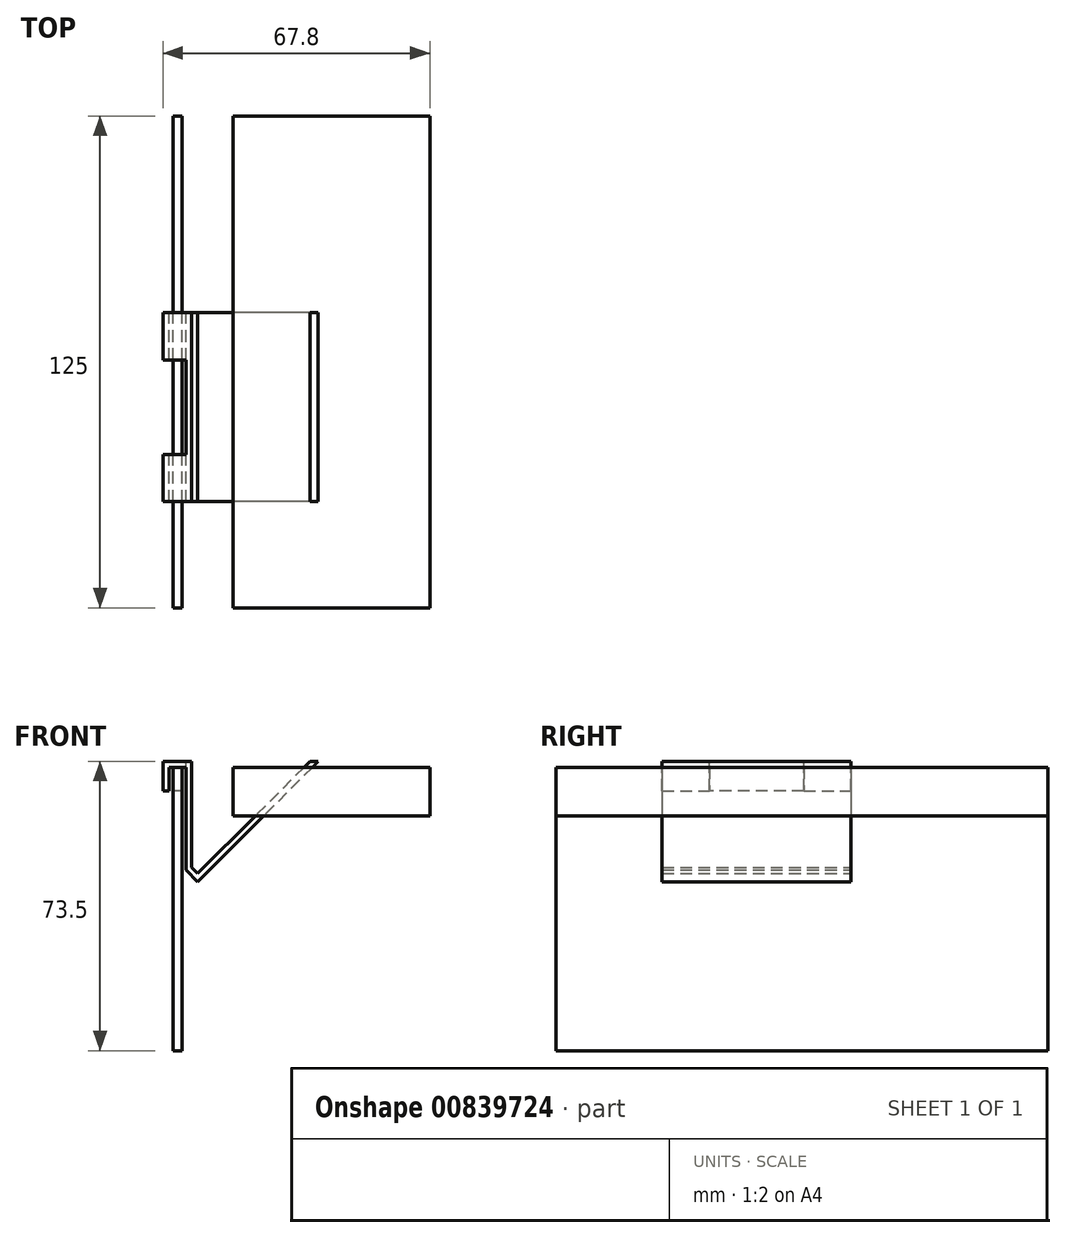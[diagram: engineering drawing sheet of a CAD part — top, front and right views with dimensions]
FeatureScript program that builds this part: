
annotation { "Feature Type Name" : "Feature", "Feature Type Description" : "" }
export const myFeature = defineFeature(function(context is Context, id is Id, definition is map)
    precondition{}
    {
        {
            var Q0;
            Q0=qCreatedBy(makeId("Front.planeOp"),FACE);
            var sketch = newSketch(context, id + "F0", { "sketchPlane" : qUnion([Q0])});
            skLineSegment(sketch, "E0", {"start": v(0, 96.34) * mm, "end": v(0, -110.81) * mm, "construction": true});
            skLineSegment(sketch, "E1", {"start": v(82.17, 0) * mm, "end": v(-88.3, 0) * mm, "construction": true});
            skSolve(sketch);
        }
        {
            var Q0;
            Q0=qCreatedBy(makeId("Front.planeOp"),FACE);
            var sketch = newSketch(context, id + "F1", { "sketchPlane" : qUnion([Q0])});
            skLineSegment(sketch, "E2.top", {"start": v(0, -72) * mm, "end": v(-2.3, -72) * mm});
            skLineSegment(sketch, "E2.left", {"start": v(0, 0) * mm, "end": v(0, -72) * mm});
            skLineSegment(sketch, "E2.right", {"start": v(-2.3, 0) * mm, "end": v(-2.3, -72) * mm});
            skLineSegment(sketch, "E3", {"start": v(-2.3, 0) * mm, "end": v(0, 0) * mm});
            skSolve(sketch);
        }
        {
            var Q0;
            Q0 = qSketchRegion(id + "F1", true);
            extrude(context, id + "F2", {"entities" : qUnion([Q0]), "depth" : 75 * mm, "offsetDistance" : 25 * mm, "hasSecondDirection" : true, "secondDirectionOppositeDirection" : true, "secondDirectionDepth" : 50 * mm});
        }
        {
            var Q0;
            Q0=qCreatedBy(makeId("Front.planeOp"),FACE);
            var sketch = newSketch(context, id + "F3", { "sketchPlane" : qUnion([Q0])});
            skLineSegment(sketch, "E4.bottom", {"start": v(13, 0) * mm, "end": v(63, 0) * mm});
            skLineSegment(sketch, "E4.top", {"start": v(13, -12.35) * mm, "end": v(63, -12.35) * mm});
            skLineSegment(sketch, "E4.left", {"start": v(13, 0) * mm, "end": v(13, -12.35) * mm});
            skLineSegment(sketch, "E4.right", {"start": v(63, 0) * mm, "end": v(63, -12.35) * mm});
            skSolve(sketch);
        }
        {
            var Q0;
            Q0 = qSketchRegion(id + "F3", true);
            extrude(context, id + "F4", {"entities" : qUnion([Q0]), "depth" : 75 * mm, "offsetDistance" : 25 * mm, "hasSecondDirection" : true, "secondDirectionOppositeDirection" : true, "secondDirectionDepth" : 50 * mm});
        }
        {
            var Q0;
            Q0=qCreatedBy(makeId("Front.planeOp"),FACE);
            var sketch = newSketch(context, id + "F5", { "sketchPlane" : qUnion([Q0])});
            skLineSegment(sketch, "E5.top", {"start": v(-4.8, -6) * mm, "end": v(-3.3, -6) * mm});
            skLineSegment(sketch, "E5.right", {"start": v(-3.3, 0) * mm, "end": v(-3.3, -6) * mm});
            skLineSegment(sketch, "E6.left", {"start": v(2.5, 1.5) * mm, "end": v(2.5, -25.5) * mm});
            skLineSegment(sketch, "E6.right", {"start": v(1, 0) * mm, "end": v(1, -26.12) * mm});
            skLineSegment(sketch, "E7", {"start": v(-4.8, 1.5) * mm, "end": v(2.5, 1.5) * mm});
            skLineSegment(sketch, "E8", {"start": v(-4.8, -6) * mm, "end": v(-4.8, 1.5) * mm});
            skLineSegment(sketch, "E9", {"start": v(-3.3, 0) * mm, "end": v(1, 0) * mm});
            skLineSegment(sketch, "E10.bottom", {"start": v(32.5, 1.5) * mm, "end": v(34.62, 1.5) * mm});
            skLineSegment(sketch, "E10.left", {"start": v(32.5, 1.5) * mm, "end": v(4, -27) * mm});
            skLineSegment(sketch, "E10.right", {"start": v(34.62, 1.5) * mm, "end": v(4, -29.12) * mm});
            skLineSegment(sketch, "E11", {"start": v(1, -26.12) * mm, "end": v(4, -29.12) * mm});
            skLineSegment(sketch, "E12", {"start": v(2.5, -25.5) * mm, "end": v(4, -27) * mm});
            skPoint(sketch, "E13.orphan", {"position": v(2.5, -28.5) * mm});
            skSolve(sketch);
        }
        {
            var Q0;
            Q0 = qSketchRegion(id + "F5", true);
            extrude(context, id + "F6", {"entities" : qUnion([Q0]), "depth" : 48 * mm, "offsetDistance" : 25 * mm});
        }
        {
            var Q0;
            Q0=makeQuery(id+"F6.opExtrude","SWEPT_FACE",FACE,{"disambiguationData":[OSD([sQuery(id+"F5.wireOp",EDGE,"E8")])]});
            var sketch = newSketch(context, id + "F7", { "sketchPlane" : qUnion([Q0])});
            skLineSegment(sketch, "E14.bottom", {"start": v(12, -6) * mm, "end": v(36, -6) * mm});
            skLineSegment(sketch, "E14.top", {"start": v(12, 1.5) * mm, "end": v(36, 1.5) * mm});
            skLineSegment(sketch, "E14.left", {"start": v(12, -6) * mm, "end": v(12, 1.5) * mm});
            skLineSegment(sketch, "E14.right", {"start": v(36, -6) * mm, "end": v(36, 1.5) * mm});
            skSolve(sketch);
        }
        {
            var Q0;
            Q0 = qSketchRegion(id + "F7", true);
            var Q1;
            Q1=makeQuery(id+"F6.opExtrude","SWEPT_FACE",FACE,{"disambiguationData":[OSD([sQuery(id+"F5.wireOp",EDGE,"E6.right")])]});
            extrude(context, id + "F8", {"entities" : qUnion([Q0]), "operationType" : NewBodyOperationType.REMOVE, "endBound" : BoundingType.UP_TO_SURFACE, "oppositeDirection" : true, "depth" : 25 * mm, "endBoundEntityFace" : qUnion([Q1]), "offsetDistance" : 25 * mm});
        }
    });
